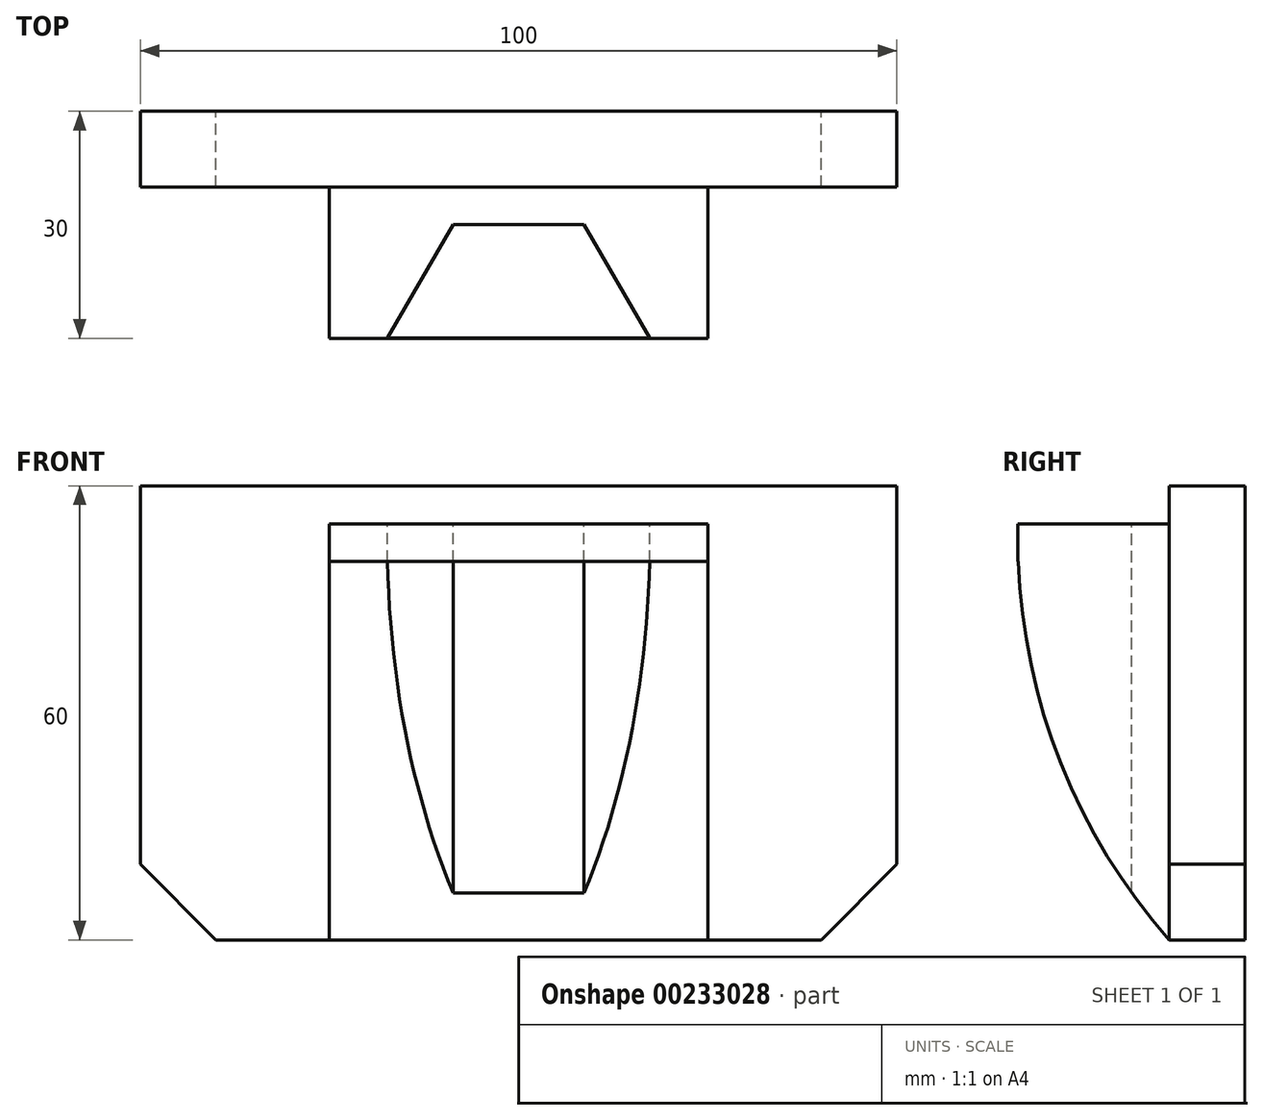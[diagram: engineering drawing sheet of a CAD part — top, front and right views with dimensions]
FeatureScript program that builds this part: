
annotation { "Feature Type Name" : "Feature", "Feature Type Description" : "" }
export const myFeature = defineFeature(function(context is Context, id is Id, definition is map)
    precondition{}
    {
        {
            var Q0;
            Q0=qCreatedBy(makeId("Front.planeOp"),FACE);
            var sketch = newSketch(context, id + "F0", { "sketchPlane" : qUnion([Q0])});
            skLineSegment(sketch, "E0", {"start": v(0, 37.37) * mm, "end": v(-50, 37.37) * mm});
            skLineSegment(sketch, "E1", {"start": v(-50, 37.37) * mm, "end": v(-50, -12.63) * mm});
            skLineSegment(sketch, "E2", {"start": v(-50, -12.63) * mm, "end": v(-40, -22.63) * mm});
            skLineSegment(sketch, "E3", {"start": v(-40, -22.63) * mm, "end": v(0, -22.63) * mm});
            skLineSegment(sketch, "E4.MirrorCS", {"start": v(0, 37.37) * mm, "end": v(50, 37.37) * mm});
            skLineSegment(sketch, "E5.MirrorCS", {"start": v(50, 37.37) * mm, "end": v(50, -12.63) * mm});
            skLineSegment(sketch, "E6.MirrorCS", {"start": v(50, -12.63) * mm, "end": v(40, -22.63) * mm});
            skLineSegment(sketch, "E7.MirrorCS", {"start": v(40, -22.63) * mm, "end": v(0, -22.63) * mm});
            skLineSegment(sketch, "E8", {"start": v(-25, 32.37) * mm, "end": v(25, 32.37) * mm});
            skLineSegment(sketch, "E9", {"start": v(-25, 32.37) * mm, "end": v(-25, -22.63) * mm});
            skLineSegment(sketch, "E10", {"start": v(25, 32.37) * mm, "end": v(25, -22.63) * mm});
            skSolve(sketch);
        }
        {
            var Q0;
            Q0=makeQuery(id+"F0.imprint","IMPRINT",FACE,{"disambiguationData":[TD([[makeQuery(id+"F0.imprint","IMPRINT",EDGE,{"derivedFrom":sQuery(id+"F0.wireOp",EDGE,"E0")}),1.0]])]});
            extrude(context, id + "F1", {"entities" : qUnion([Q0]), "depth" : 10 * mm});
        }
        {
            var Q0;
            Q0=makeQuery(id+"F0.imprint","IMPRINT",FACE,{"disambiguationData":[TD([[makeQuery(id+"F0.imprint","IMPRINT",EDGE,{"derivedFrom":sQuery(id+"F0.wireOp",EDGE,"E8")}),-1.0]])]});
            extrude(context, id + "F2", {"entities" : qUnion([Q0]), "operationType" : NewBodyOperationType.ADD, "depth" : 30 * mm});
        }
        {
            var Q0;
            Q0=makeQuery(id+"F2.opExtrude","SWEPT_FACE",FACE,{"disambiguationData":[OSD([sQuery(id+"F0.wireOp",EDGE,"E10")])]});
            var sketch = newSketch(context, id + "F3", { "sketchPlane" : qUnion([Q0])});
            skLineSegment(sketch, "E11.0", {"start": v(-30, 32.37) * mm, "end": v(-30, -22.63) * mm});
            skLineSegment(sketch, "E11.1", {"start": v(-30, -22.63) * mm, "end": v(-10, -22.63) * mm});
            skLineSegment(sketch, "E11.3", {"start": v(-30, 32.37) * mm, "end": v(-10, 32.37) * mm});
            skLineSegment(sketch, "E11.4", {"start": v(-10, 37.37) * mm, "end": v(-10, -12.63) * mm});
            skPoint(sketch, "E11.5", {"position": v(-20, -22.63) * mm});
            skLineSegment(sketch, "E12", {"start": v(-10, -22.63) * mm, "end": v(-10, 32.37) * mm});
            skLineSegment(sketch, "E13", {"start": v(-10, 32.37) * mm, "end": v(-30, 32.37) * mm});
            skLineSegment(sketch, "E14", {"start": v(-30, 32.37) * mm, "end": v(-30, 27.37) * mm});
            skLineSegment(sketch, "E15", {"start": v(-30, 27.37) * mm, "end": v(-25, 27.37) * mm});
            skLineSegment(sketch, "E16", {"start": v(-25, 27.37) * mm, "end": v(-25, 32.37) * mm});
            skArc(sketch, "E17", {"start": v(-29.95, 27.37) * mm, "mid": v(-24.3, 0.64) * mm, "end": v(-10, -22.63) * mm});
            skSolve(sketch);
        }
        {
            var Q0;
            {var subQ3=sQuery(id+"F3.wireOp",EDGE,"E14");Q0=makeQuery(id+"F3.imprint","IMPRINT",FACE,{"disambiguationData":[TD([[makeQuery(id+"F3.imprint","IMPRINT",EDGE,{"derivedFrom":subQ3}),1.0]])]});}
            var Q1;
            {var subQ0=sQuery(id+"F3.wireOp",EDGE,"E11.0");Q1=makeQuery(id+"F3.imprint","IMPRINT",FACE,{"disambiguationData":[TD([[makeQuery(id+"F3.imprint","IMPRINT",EDGE,{"derivedFrom":subQ0}),1.0]])]});}
            extrude(context, id + "F4", {"entities" : qUnion([Q0, Q1]), "operationType" : NewBodyOperationType.REMOVE, "endBound" : BoundingType.THROUGH_ALL, "oppositeDirection" : true, "depth" : 25 * mm});
        }
        {
            var Q0;
            Q0=makeQuery(id+"F2.opExtrude","SWEPT_FACE",FACE,{"disambiguationData":[OSD([sQuery(id+"F0.wireOp",EDGE,"E8")])]});
            var sketch = newSketch(context, id + "F5", { "sketchPlane" : qUnion([Q0])});
            skLineSegment(sketch, "E18.0", {"start": v(25, -25) * mm, "end": v(25, -10) * mm});
            skLineSegment(sketch, "E18.1", {"start": v(25, -29.95) * mm, "end": v(25, -25) * mm});
            skLineSegment(sketch, "E18.2", {"start": v(-25, -29.95) * mm, "end": v(25, -29.95) * mm});
            skLineSegment(sketch, "E18.3", {"start": v(-25, -29.95) * mm, "end": v(-25, -25) * mm});
            skLineSegment(sketch, "E18.4", {"start": v(-25, -25) * mm, "end": v(-25, -10) * mm});
            skLineSegment(sketch, "E18.5", {"start": v(-50, -10) * mm, "end": v(50, -10) * mm});
            skCircle(sketch, "E19", {"center": v(0, -29.95) * mm, "radius": 15 * mm, "construction": true});
            skLineSegment(sketch, "E20", {"start": v(-17.32, -29.95) * mm, "end": v(-8.66, -14.95) * mm});
            skLineSegment(sketch, "E21", {"start": v(-8.66, -14.95) * mm, "end": v(8.66, -14.95) * mm});
            skLineSegment(sketch, "E22", {"start": v(8.66, -14.95) * mm, "end": v(17.32, -29.95) * mm});
            skLineSegment(sketch, "E23", {"start": v(17.32, -29.95) * mm, "end": v(0, -29.95) * mm});
            skLineSegment(sketch, "E24", {"start": v(0, -29.95) * mm, "end": v(-17.32, -29.95) * mm});
            skSolve(sketch);
        }
        {
            var Q0;
            {var subQ0=sQuery(id+"F5.wireOp",EDGE,"E21");Q0=makeQuery(id+"F5.imprint","IMPRINT",FACE,{"disambiguationData":[TD([[makeQuery(id+"F5.imprint","IMPRINT",EDGE,{"derivedFrom":subQ0}),-1.0]])]});}
            var Q1;
            {var subQ5=sQuery(id+"F5.wireOp",EDGE,"E23");Q1=makeQuery(id+"F5.imprint","IMPRINT",FACE,{"disambiguationData":[TD([[makeQuery(id+"F5.imprint","IMPRINT",EDGE,{"derivedFrom":subQ5}),-1.0]])]});}
            extrude(context, id + "F6", {"entities" : qUnion([Q0, Q1]), "operationType" : NewBodyOperationType.REMOVE, "endBound" : BoundingType.THROUGH_ALL, "oppositeDirection" : true, "depth" : 25 * mm});
        }
    });
